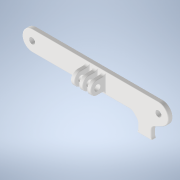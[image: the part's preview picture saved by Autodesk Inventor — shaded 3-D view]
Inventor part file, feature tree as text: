
AUTODESK INVENTOR PART (.ipt)
format: ipt  version: 2021.3 (Build 253353010, 353A)  size: 345,088 bytes
history: native  units: mm
features: reference x5, extrude x3, fillet x3, sketch x3, other x2, projected_geometry x1
ambient origin geometry x8: Origin, YZ Plane, XZ Plane, XY Plane, X Axis, Y Axis, Z Axis, Center Point
bodies: Volumenkörper1 (feature_tree)
feature tree (17):
  extrude  "Extrusion1"  Depth=4.5mm
  extrude  "Extrusion2"  Depth=10.0mm
  extrude  "Extrusion3"  Depth=10.0mm
  fillet  "Rundung1"  Radius=10.0mm
  fillet  "Rundung3"  Radius=11.0mm
  fillet  "Rundung4"  Radius=4.5mm
  sketch  "Skizze2"  dims[d3=4.5mm d4=4.5mm]
  reference  "Referenz2"
  reference  "Referenz3"
  reference  "Referenz4"
  sketch  "Skizze3"  dims[d5=3.0mm d6=0.0mm d7=10.0mm]
  sketch  "Skizze4"  dims[d8=3.0mm d9=20.0mm d11=6.07mm d12=10.0mm d14=10.0mm d16=20.0mm d18=6.07mm d19=10.0mm d21=10.0mm d23=11.0mm d24=0.0mm d25=4.5mm d26=10.0mm d27=0.0mm d28=10.0mm d29=4.5mm d30=1.0mm d48=2.0mm d49=4.0mm d50=2.0mm d51=0.5mm d53=0.5mm d54=15.0mm d55=4.0mm d59=135.0deg d61=0.5mm]
  projected_geometry  "Projizierte Kontur1"
  reference  "Referenz5"
  reference  "Referenz6"
  other  "Baugruppe18"
  other  "Intel_RealSense_D455_CAD_external_v2:1"
